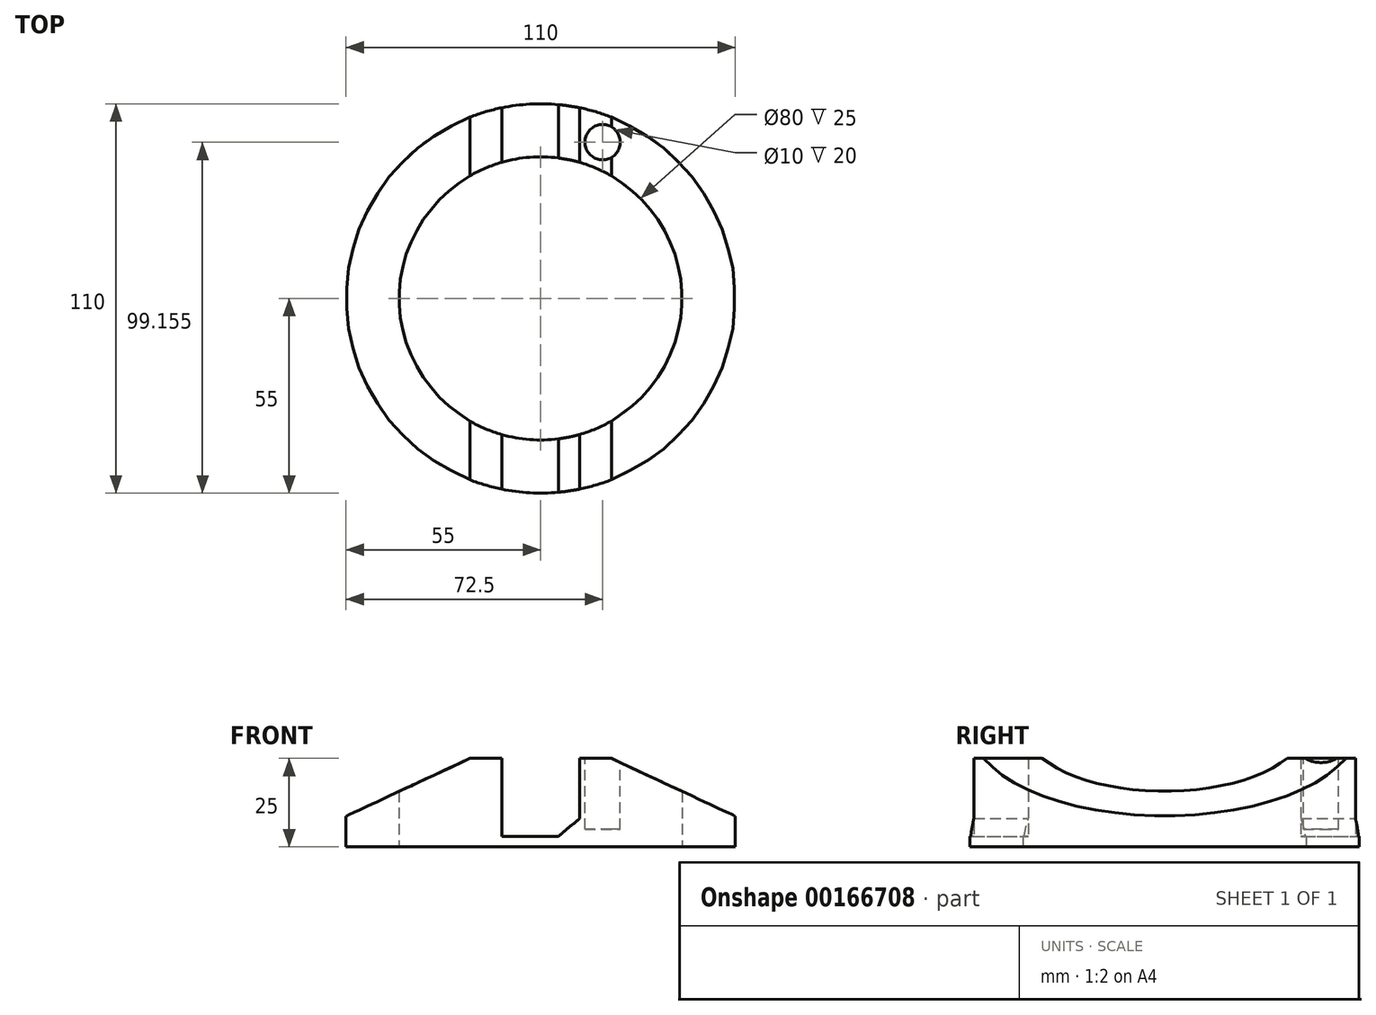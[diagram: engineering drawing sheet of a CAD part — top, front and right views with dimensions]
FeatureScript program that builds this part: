
annotation { "Feature Type Name" : "Feature", "Feature Type Description" : "" }
export const myFeature = defineFeature(function(context is Context, id is Id, definition is map)
    precondition{}
    {
        {
            var Q0;
            Q0=qCreatedBy(makeId("Top.planeOp"),FACE);
            var sketch = newSketch(context, id + "F0", { "sketchPlane" : qUnion([Q0])});
            skArc(sketch, "E0", {"start": v(39.92, 2.5) * mm, "mid": v(-40, 0) * mm, "end": v(39.92, -2.5) * mm});
            skCircle(sketch, "E1", {"center": v(0, 0) * mm, "radius": 55 * mm});
            skArc(sketch, "E2", {"start": v(39.92, -2.5) * mm, "mid": v(40, 0) * mm, "end": v(39.92, 2.5) * mm});
            skSolve(sketch);
        }
        {
            var Q0;
            Q0 = qSketchRegion(id + "F0", true);
            extrude(context, id + "F1", {"entities" : qUnion([Q0]), "depth" : 25 * mm});
        }
        {
            var Q0;
            Q0=qCreatedBy(makeId("Front.planeOp"),FACE);
            var sketch = newSketch(context, id + "F2", { "sketchPlane" : qUnion([Q0])});
            skLineSegment(sketch, "E3.0", {"start": v(-55, 25) * mm, "end": v(55, 25) * mm, "construction": true});
            skLineSegment(sketch, "E4", {"start": v(20, 25) * mm, "end": v(62.9, 5) * mm});
            skLineSegment(sketch, "E5", {"start": v(62.9, 5) * mm, "end": v(62.9, 25) * mm});
            skLineSegment(sketch, "E6", {"start": v(62.9, 25) * mm, "end": v(20, 25) * mm});
            skLineSegment(sketch, "E7.MirrorCS", {"start": v(-20, 25) * mm, "end": v(-62.9, 5) * mm});
            skLineSegment(sketch, "E8.MirrorCS", {"start": v(55, 25) * mm, "end": v(-55, 25) * mm, "construction": true});
            skLineSegment(sketch, "E9.MirrorCS", {"start": v(-62.9, 25) * mm, "end": v(-20, 25) * mm});
            skLineSegment(sketch, "E10.MirrorCS", {"start": v(-62.9, 5) * mm, "end": v(-62.9, 25) * mm});
            skSolve(sketch);
        }
        {
            var Q0;
            Q0 = qSketchRegion(id + "F2", true);
            extrude(context, id + "F3", {"entities" : qUnion([Q0]), "operationType" : NewBodyOperationType.REMOVE, "endBound" : BoundingType.THROUGH_ALL, "oppositeDirection" : true, "depth" : 25 * mm, "hasSecondDirection" : true, "secondDirectionBound" : SecondDirectionBoundingType.THROUGH_ALL, "secondDirectionOppositeDirection" : false, "secondDirectionDepth" : 25 * mm});
        }
        {
            var Q0;
            Q0=qCreatedBy(makeId("Front.planeOp"),FACE);
            var sketch = newSketch(context, id + "F4", { "sketchPlane" : qUnion([Q0])});
            skLineSegment(sketch, "E11", {"start": v(-11, 25) * mm, "end": v(-11, 3) * mm});
            skLineSegment(sketch, "E12", {"start": v(-11, 3) * mm, "end": v(5, 3) * mm});
            skLineSegment(sketch, "E13", {"start": v(5, 3) * mm, "end": v(11, 8) * mm});
            skLineSegment(sketch, "E14", {"start": v(11, 8) * mm, "end": v(11, 25) * mm});
            skLineSegment(sketch, "E15", {"start": v(11, 25) * mm, "end": v(-11, 25) * mm});
            skPoint(sketch, "E16", {"position": v(0, 25) * mm});
            skSolve(sketch);
        }
        {
            var Q0;
            Q0 = qSketchRegion(id + "F4", true);
            extrude(context, id + "F5", {"entities" : qUnion([Q0]), "operationType" : NewBodyOperationType.REMOVE, "endBound" : BoundingType.THROUGH_ALL, "depth" : 25 * mm, "hasSecondDirection" : true, "secondDirectionBound" : SecondDirectionBoundingType.THROUGH_ALL, "secondDirectionOppositeDirection" : true, "secondDirectionDepth" : 25 * mm});
        }
        {
            var Q0;
            {var subQ0=sQuery(id+"F0.wireOp",EDGE,"E0");var subQ1=sQuery(id+"F0.wireOp",EDGE,"E1");Q0=makeQuery(id+"F5.boolean.opBoolean","SPLIT",FACE,{"disambiguationData":[TD([makeQuery(id+"F3.boolean.opBoolean","COPY",FACE,{"derivedFrom":makeQuery(id+"F3.opExtrude","SWEPT_FACE",FACE,{"disambiguationData":[OSD([sQuery(id+"F2.wireOp",EDGE,"E4")])]})})])],"derivedFrom":makeQuery(id+"F3.boolean.opBoolean","SPLIT",FACE,{"disambiguationData":[OD(0.0)],"derivedFrom":makeQuery(id+"F1.opExtrude","CAP_FACE",FACE,{"disambiguationData":[OSD([subQ0,subQ1])],"isStart":false})})});}
            var sketch = newSketch(context, id + "F6", { "sketchPlane" : qUnion([Q0])});
            skCircle(sketch, "E17", {"center": v(17.5, 44.15) * mm, "radius": 5 * mm});
            skLineSegment(sketch, "E18", {"start": v(11, -46.17) * mm, "end": v(39.22, -54.94) * mm});
            skLineSegment(sketch, "E19", {"start": v(15.27, 36.97) * mm, "end": v(19.73, 51.34) * mm, "construction": true});
            skArc(sketch, "E20.0", {"start": v(20, 51.23) * mm, "mid": v(55, 0) * mm, "end": v(20, -51.23) * mm, "construction": true});
            skLineSegment(sketch, "E21.0", {"start": v(11, 38.46) * mm, "end": v(11, 53.89) * mm, "construction": true});
            skLineSegment(sketch, "E22", {"start": v(11, 46.17) * mm, "end": v(40.75, 36.93) * mm, "construction": true});
            skSolve(sketch);
        }
        {
            var Q0;
            Q0=makeQuery(id+"F1.opExtrude","CAP_FACE",FACE,{"disambiguationData":[OSD([sQuery(id+"F0.wireOp",EDGE,"E0"),sQuery(id+"F0.wireOp",EDGE,"E1")])],"isStart":true});
            cPlane(context, id + "F7", {"entities" : qUnion([Q0]), "cplaneType" : CPlaneType.OFFSET, "offset" : 5 * mm, "oppositeDirection" : true, "width" : 150 * mm, "height" : 150 * mm});
        }
        {
            var Q0;
            Q0 = qSketchRegion(id + "F6", true);
            var Q1;
            Q1=qCreatedBy(id+"F7.planeOp",FACE);
            extrude(context, id + "F8", {"entities" : qUnion([Q0]), "operationType" : NewBodyOperationType.REMOVE, "endBound" : BoundingType.UP_TO_SURFACE, "oppositeDirection" : true, "endBoundEntityFace" : qUnion([Q1]), "depth" : 25 * mm});
        }
    });
